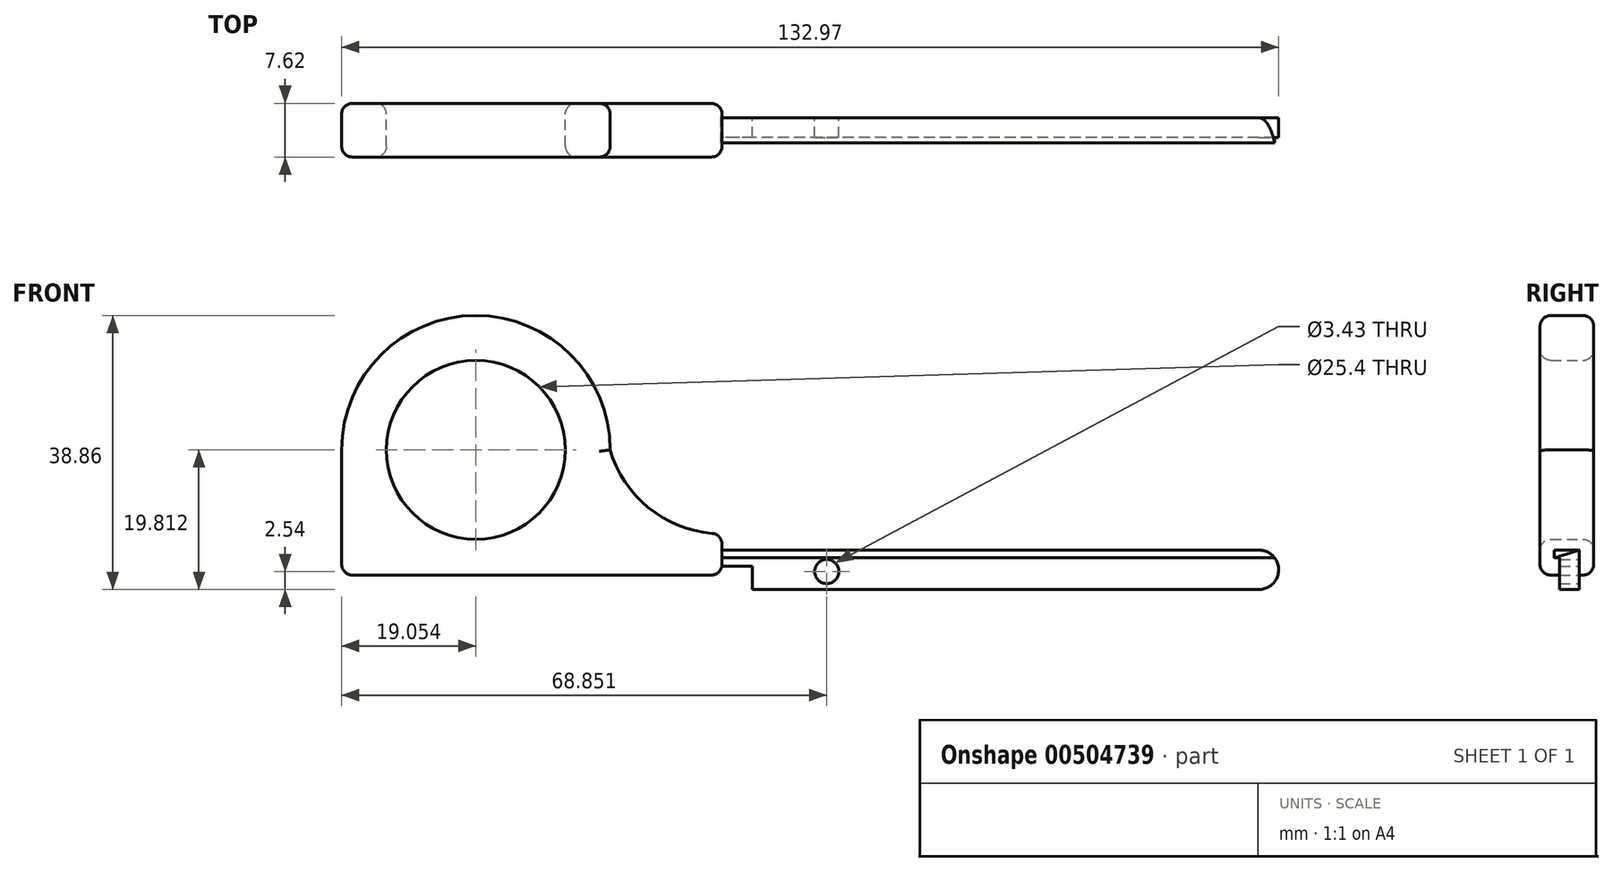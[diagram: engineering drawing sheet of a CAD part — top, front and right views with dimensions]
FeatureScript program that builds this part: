
annotation { "Feature Type Name" : "Feature", "Feature Type Description" : "" }
export const myFeature = defineFeature(function(context is Context, id is Id, definition is map)
    precondition{}
    {
        {
            var Q0;
            Q0=qCreatedBy(makeId("Front.planeOp"),FACE);
            var sketch = newSketch(context, id + "F0", { "sketchPlane" : qUnion([Q0])});
            skLineSegment(sketch, "E0", {"start": v(-53.86, -34.26) * mm, "end": v(-53.86, -16.48) * mm});
            skLineSegment(sketch, "E1", {"start": v(-53.86, -34.26) * mm, "end": v(0.12, -34.26) * mm});
            skLineSegment(sketch, "E2", {"start": v(0.12, -34.26) * mm, "end": v(0.12, -28.4) * mm});
            skLineSegment(sketch, "E3", {"start": v(0.12, -30.7) * mm, "end": v(76.32, -30.7) * mm});
            skArc(sketch, "E4", {"start": v(-15.76, -16.48) * mm, "mid": v(-34.8, 2.57) * mm, "end": v(-53.86, -16.48) * mm});
            skArc(sketch, "E5", {"start": v(-15.76, -16.48) * mm, "mid": v(-9.8, -25.09) * mm, "end": v(0.12, -28.4) * mm});
            skCircle(sketch, "E6", {"center": v(-34.8, -16.48) * mm, "radius": 12.7 * mm});
            skLineSegment(sketch, "E7", {"start": v(4.44, -32.99) * mm, "end": v(0.12, -32.99) * mm});
            skArc(sketch, "E8", {"start": v(76.32, -36.29) * mm, "mid": v(79.11, -33.5) * mm, "end": v(76.32, -30.7) * mm});
            skLineSegment(sketch, "E9", {"start": v(76.32, -36.29) * mm, "end": v(4.45, -36.29) * mm});
            skLineSegment(sketch, "E10", {"start": v(4.45, -36.29) * mm, "end": v(4.44, -32.99) * mm});
            skCircle(sketch, "E11", {"center": v(15, -33.75) * mm, "radius": 1.71 * mm});
            skSolve(sketch);
        }
        {
            var Q0;
            Q0=makeQuery(id+"F0.imprint","IMPRINT",FACE,{"disambiguationData":[TD([[makeQuery(id+"F0.imprint","IMPRINT",EDGE,{"derivedFrom":sQuery(id+"F0.wireOp",EDGE,"E0")}),-1.0]])]});
            extrude(context, id + "F1", {"entities" : qUnion([Q0]), "endBound" : BoundingType.SYMMETRIC, "depth" : 7.62 * mm});
        }
        {
            var Q0;
            {var subQ1=sQuery(id+"F0.wireOp",EDGE,"E3");Q0=makeQuery(id+"F0.imprint","IMPRINT",FACE,{"disambiguationData":[TD([[makeQuery(id+"F0.imprint","IMPRINT",EDGE,{"derivedFrom":subQ1}),-1.0]])]});}
            extrude(context, id + "F2", {"entities" : qUnion([Q0]), "operationType" : NewBodyOperationType.ADD, "endBound" : BoundingType.SYMMETRIC, "depth" : 3.56 * mm});
        }
        {
            var Q0;
            Q0=makeQuery(id+"F1.opExtrude","CAP_EDGE",EDGE,{"disambiguationData":[OSD([sQuery(id+"F0.wireOp",EDGE,"E6")])],"isStart":false});
            var Q1;
            Q1=makeQuery(id+"F1.opExtrude","CAP_EDGE",EDGE,{"disambiguationData":[OSD([sQuery(id+"F0.wireOp",EDGE,"E6")])],"isStart":true});
            var Q2;
            Q2=makeQuery(id+"F1.opExtrude","CAP_EDGE",EDGE,{"disambiguationData":[OSD([sQuery(id+"F0.wireOp",EDGE,"E0")])],"isStart":true});
            var Q3;
            Q3=makeQuery(id+"F1.opExtrude","CAP_EDGE",EDGE,{"disambiguationData":[OSD([sQuery(id+"F0.wireOp",EDGE,"E0")])],"isStart":false});
            var Q4;
            Q4=makeQuery(id+"F1.opExtrude","SWEPT_EDGE",EDGE,{"disambiguationData":[OSD([sQuery(id+"F0.wireOp",EDGE,"E0"),sQuery(id+"F0.wireOp",EDGE,"E1")])]});
            var Q5;
            Q5=makeQuery(id+"F1.opExtrude","CAP_EDGE",EDGE,{"disambiguationData":[OSD([sQuery(id+"F0.wireOp",EDGE,"E1")])],"isStart":false});
            var Q6;
            Q6=makeQuery(id+"F1.opExtrude","CAP_EDGE",EDGE,{"disambiguationData":[OSD([sQuery(id+"F0.wireOp",EDGE,"E1")])],"isStart":true});
            var Q7;
            Q7=makeQuery(id+"F1.opExtrude","CAP_EDGE",EDGE,{"disambiguationData":[OSD([sQuery(id+"F0.wireOp",EDGE,"E4")])],"isStart":false});
            var Q8;
            Q8=makeQuery(id+"F1.opExtrude","CAP_EDGE",EDGE,{"disambiguationData":[OSD([sQuery(id+"F0.wireOp",EDGE,"E4")])],"isStart":true});
            var Q9;
            Q9=makeQuery(id+"F1.opExtrude","CAP_EDGE",EDGE,{"disambiguationData":[OSD([sQuery(id+"F0.wireOp",EDGE,"E5")])],"isStart":true});
            var Q10;
            Q10=makeQuery(id+"F1.opExtrude","CAP_EDGE",EDGE,{"disambiguationData":[OSD([sQuery(id+"F0.wireOp",EDGE,"E5")])],"isStart":false});
            var Q11;
            Q11=makeQuery(id+"F1.opExtrude","CAP_EDGE",EDGE,{"disambiguationData":[OSD([sQuery(id+"F0.wireOp",EDGE,"E2")])],"isStart":false});
            var Q12;
            Q12=makeQuery(id+"F1.opExtrude","SWEPT_EDGE",EDGE,{"disambiguationData":[OSD([sQuery(id+"F0.wireOp",EDGE,"E2"),sQuery(id+"F0.wireOp",EDGE,"E5")])]});
            var Q13;
            Q13=makeQuery(id+"F1.opExtrude","CAP_EDGE",EDGE,{"disambiguationData":[OSD([sQuery(id+"F0.wireOp",EDGE,"E2")])],"isStart":true});
            var Q14;
            Q14=makeQuery(id+"F1.opExtrude","SWEPT_EDGE",EDGE,{"disambiguationData":[OSD([sQuery(id+"F0.wireOp",EDGE,"E1"),sQuery(id+"F0.wireOp",EDGE,"E2")])]});
            fillet(context, id + "F3", {"entities" : qUnion([Q0, Q1, Q2, Q3, Q4, Q5, Q6, Q7, Q8, Q9, Q10, Q11, Q12, Q13, Q14]), "radius" : 1.52 * mm, "tangentPropagation" : true, "allowEdgeOverflow" : false});
        }
        {
            var Q0;
            Q0=qCreatedBy(makeId("Right.planeOp"),FACE);
            var sketch = newSketch(context, id + "F4", { "sketchPlane" : qUnion([Q0])});
            skLineSegment(sketch, "E12", {"start": v(-1.8, -31.82) * mm, "end": v(1.82, -30.69) * mm});
            skLineSegment(sketch, "E13", {"start": v(1.82, -30.69) * mm, "end": v(-1.8, -30.69) * mm});
            skLineSegment(sketch, "E14", {"start": v(-1.8, -30.69) * mm, "end": v(-1.8, -31.82) * mm});
            skSolve(sketch);
        }
        {
            var Q0;
            Q0=makeQuery(id+"F4.imprint","IMPRINT",FACE,{"disambiguationData":[TD([[makeQuery(id+"F4.imprint","IMPRINT",EDGE,{"derivedFrom":sQuery(id+"F4.wireOp",EDGE,"E12")}),1.0]])]});
            extrude(context, id + "F5", {"entities" : qUnion([Q0]), "operationType" : NewBodyOperationType.REMOVE, "depth" : 99.57 * mm});
        }
        {
            var Q0;
            Q0=makeQuery(id+"F2.opExtrude","CAP_FACE",FACE,{"disambiguationData":[OSD([sQuery(id+"F0.wireOp",EDGE,"E2"),sQuery(id+"F0.wireOp",EDGE,"E3"),sQuery(id+"F0.wireOp",EDGE,"E7"),sQuery(id+"F0.wireOp",EDGE,"E8"),sQuery(id+"F0.wireOp",EDGE,"E9"),sQuery(id+"F0.wireOp",EDGE,"E10"),sQuery(id+"F0.wireOp",EDGE,"E11")])],"isStart":false});
            extrude(context, id + "F6", {"entities" : qUnion([Q0]), "operationType" : NewBodyOperationType.ADD, "depth" : 51.56 * mm});
        }
        {
            var Q0;
            Q0=makeQuery(id+"F6.opExtrude","CAP_FACE",FACE,{"disambiguationData":[OSD([sQuery(id+"F0.wireOp",EDGE,"E2"),sQuery(id+"F0.wireOp",EDGE,"E3"),sQuery(id+"F0.wireOp",EDGE,"E7"),sQuery(id+"F0.wireOp",EDGE,"E8"),sQuery(id+"F0.wireOp",EDGE,"E9"),sQuery(id+"F0.wireOp",EDGE,"E10"),sQuery(id+"F0.wireOp",EDGE,"E11")])],"isStart":false});
            extrude(context, id + "F7", {"entities" : qUnion([Q0]), "operationType" : NewBodyOperationType.REMOVE, "oppositeDirection" : true, "depth" : 52.32 * mm, "offsetDistance" : 25.4 * mm});
        }
    });
